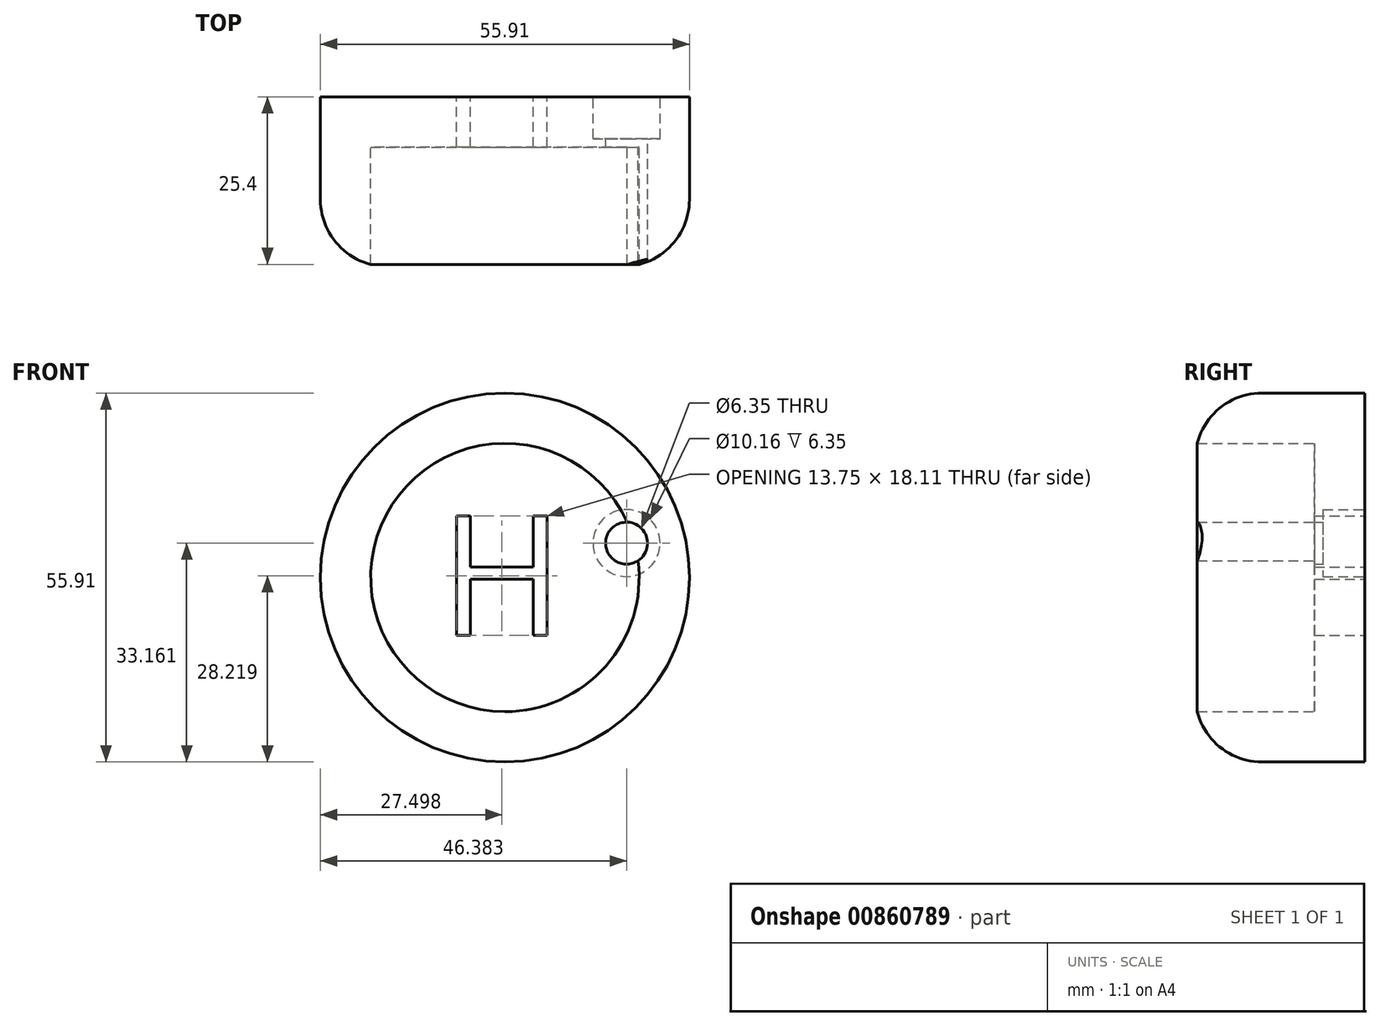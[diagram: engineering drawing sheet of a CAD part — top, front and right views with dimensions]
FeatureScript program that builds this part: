
annotation { "Feature Type Name" : "Feature", "Feature Type Description" : "" }
export const myFeature = defineFeature(function(context is Context, id is Id, definition is map)
    precondition{}
    {
        {
            var Q0;
            Q0=qCreatedBy(makeId("Front.planeOp"),FACE);
            var sketch = newSketch(context, id + "F0", { "sketchPlane" : qUnion([Q0])});
            skCircle(sketch, "E0", {"center": v(-10.13, 8.79) * mm, "radius": 27.95 * mm});
            skSolve(sketch);
        }
        {
            var Q0;
            Q0=makeQuery(id+"F0.imprint","IMPRINT",FACE,{"disambiguationData":[TD([[makeQuery(id+"F0.imprint","IMPRINT",EDGE,{"derivedFrom":sQuery(id+"F0.wireOp",EDGE,"E0")}),1.0]])]});
            extrude(context, id + "F1", {"entities" : qUnion([Q0]), "endBound" : BoundingType.SYMMETRIC, "depth" : 25.4 * mm, "offsetDistance" : 25.4 * mm});
        }
        {
            var Q0;
            Q0=makeQuery(id+"F1.opExtrude","CAP_FACE",FACE,{"disambiguationData":[OSD([sQuery(id+"F0.wireOp",EDGE,"E0")])],"isStart":false});
            shell(context, id + "F2", {"entities" : qUnion([Q0]), "thickness" : 7.62 * mm});
        }
        {
            var Q0;
            Q0=makeQuery(id+"F1.opExtrude","CAP_EDGE",EDGE,{"disambiguationData":[OSD([sQuery(id+"F0.wireOp",EDGE,"E0")])],"isStart":false});
            var Q1;
            Q1=makeQuery(id+"FE14K3zwTa7uJ4m_1.boolean.opBoolean","COPY",EDGE,{"derivedFrom":makeQuery(id+"FE14K3zwTa7uJ4m_1.opExtrude","CAP_EDGE",EDGE,{"disambiguationData":[OSD([sQuery(id+"FkVgUVTvRKIpo2t_1.wireOp",EDGE,"NU2UfjRv-lTqG-S0VV-AqSS-uAraZbosSeRs.left")])],"isStart":true})});
            fillet(context, id + "F3", {"entities" : qUnion([Q0, Q1]), "radius" : 10.12 * mm, "tangentPropagation" : true, "allowEdgeOverflow" : false});
        }
        {
            var Q0;
            Q0=makeQuery(id+"F1.opExtrude","CAP_FACE",FACE,{"disambiguationData":[OSD([sQuery(id+"F0.wireOp",EDGE,"E0")])],"isStart":true});
            var sketch = newSketch(context, id + "F4", { "sketchPlane" : qUnion([Q0])});
            skText(sketch, "E1", { "text": "H", "fontName": "OpenSans-Regular.ttf"});
            const initialGuessF4  = {"E1": [0.00123, 0, 1, 0, 0.01826]};
            skSetInitialGuess(sketch, initialGuessF4);
            skSolve(sketch);
        }
        {
            var Q0;
            Q0=makeQuery(id+"F4.imprint","IMPRINT",FACE,{"disambiguationData":[TD([[makeQuery(id+"F4.imprint","IMPRINT",EDGE,{"derivedFrom":sQuery(id+"F4.wireOp",EDGE,"E1.sketch_text.stroke-0")}),-1.0]])]});
            extrude(context, id + "F5", {"entities" : qUnion([Q0]), "operationType" : NewBodyOperationType.REMOVE, "oppositeDirection" : true, "depth" : 25.4 * mm, "offsetDistance" : 25.4 * mm});
        }
        {
            var Q0;
            Q0=makeQuery(id+"F1.opExtrude","SWEPT_BODY",BODY,{"disambiguationData":[OSD([sQuery(id+"F0.wireOp",EDGE,"E0")])]});
            transform(context, id + "F6", {"entities" : qUnion([Q0]), "transformType" : TransformType.TRANSLATION_3D, "dx" : 10.16 * mm, "dy" : 0 * mm, "dz" : -9.14 * mm, "makeCopy" : false});
        }
        {
            var Q0;
            Q0=makeQuery(id+"F1.opExtrude","CAP_FACE",FACE,{"disambiguationData":[OSD([sQuery(id+"F0.wireOp",EDGE,"E0")])],"isStart":true});
            var sketch = newSketch(context, id + "F7", { "sketchPlane" : qUnion([Q0])});
            skPoint(sketch, "E2", {"position": v(-18.45, 4.85) * mm});
            skSolve(sketch);
        }
        {
            var Q0;
            Q0=sQuery(id+"F7.wireOp",VERTEX,"E2");
            var Q1;
            Q1=makeQuery(id+"F1.opExtrude","SWEPT_BODY",BODY,{"disambiguationData":[OSD([sQuery(id+"F0.wireOp",EDGE,"E0")])]});
            hole(context, id + "F8", {"style" : HoleStyle.C_BORE, "endStyle" : HoleEndStyle.THROUGH, "holeDiameter" : 6.35 * mm, "cBoreDiameter" : 10.16 * mm, "cBoreDepth" : 6.35 * mm, "majorDiameter" : 6.35 * mm, "isTappedThrough" : true, "tappedDepth" : 12.7 * mm, "tapClearance" : 3, "locations" : qUnion([Q0]), "scope" : qUnion([Q1])});
        }
    });
